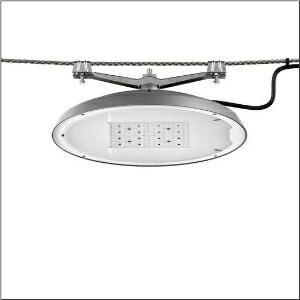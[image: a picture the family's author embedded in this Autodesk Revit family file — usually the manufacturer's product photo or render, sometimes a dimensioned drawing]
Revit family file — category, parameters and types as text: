
# Revit family: dl_50_iq_mini___st1_0s_5xa248w31f08me_2b15
name_source: partatom
category: Lighting Fixtures
units: mm (PartAtom-declared; Revit-internal decimal feet)

## family parameters
Cut with Voids When Loaded = No
Host = Face
Light Source = No
Part Type = Normal
Room Calculation Point = No
Round Connector Dimension = Use Diameter
Shared = No

## types (1)
- --- (1 x LED, 15660 lm, 107.8 W, 3000K)
    Apparent Load = 108 VA
    CIE Flux Codes = 37 72 97 100 100
    Color Rendering = 70
    Color Temperature = 3000K
    Default Elevation = 1800 mm
    Description = DL 50 iQ mini, catenary luminaire, primary light control with lens, of PMMA, primary optical cover: cover, of toughened safety glass, transparent, light distribution: ST1.0s, light emission: direct distribution, primary light characteristic: symmetric, installation type: suspended mounting, LED, High Power LED, rated luminous flux: 15.660lm, luminous efficacy: 145lm/W, light colour: 730, colour temperature: 3000K, control gear: iQ Street-Remote, control: optimised constant luminous flux control (CLO 2.0), Desk-Remote (wireless, voltage-free reading and setting of iQ features in the workshop via application-optimized NFC function/RFID function), Light-Fading, Smart-Wire, Night-Set, Lumen-Switch, Temp-Guard, Auto-Match, Street-Remote, mains connection: 230..240V, AC, 50/60Hz, start of lifetime: 108W, end of service life: 118W, reduction: 47W, luminaire housing, of diecast aluminium, powder-coated, SITECO metallic grey (DB 702S), diameter: 500mm, height: 115mm, mounting height: 4..12m, protection rating (complete): IP66, insulation class (complete): insulation class II (safety insulation), certification: CE, ENEC, ENEC+, VDE, impact resistance: IK08, permissible operating ambient temperature for outdoor applications: -25..+40°C, standard-compliant lighting for roads and squares, packaging unit: 1 piece

Light Distribution: ST1.0s
    Height = 124 mm  [stored 0.406824 ft]
    Lamp = 1 x LED
    Lamp Light Flux = 15660 lm
    Lamp Power = 107.8 W
    Lamp count = 1
    Length = 500 mm
    Luminous efficacy = 145 lm/W
    Manufacturer = Siteco
    ModVariant = No
    Model = 5XA248W31F08ME
    Number of Poles = 1
    OnlyDefault = Yes
    Power Factor = 1
    Product Name = DL 50 iQ mini | ST1.0s
    Product group = catenary luminaire
    ProductGroupID = 6300
    Protection Class = Protection class II
    Protection Degree = IP 66
    RLX_Detail_Level = 1
    RLX_Emergency_Light_Flux = 0 lm
    RLX_Emergency_Type = 0
    RLX_Emergency_Type_DB = No
    RlxData = <blob elided: 127317 chars, md5=70cb6eed>
    Socket = socket
    Standby Power = 0 W
    System Light Flux = 15660 lm
    System Power = 108 W
    Type Comments = factory setting: luminous flux: 100 % | dim-lin: 254 | 565 mA
    Type Image = l_1251783.jpg
    URL = http://relux.com
    VarID = @adj_139907
    Voltage = 0 V
    Weight = 0.00 kg
    Width = 0 mm  [stored 0 ft]

note: [stored X ft] marks values corroborated as IEEE doubles in the binary element streams (Revit-internal decimal feet)

## geometry (parser evidence)
native form markers: Blend x4, Sweep x14
no freeform markers — native parametric forms only
